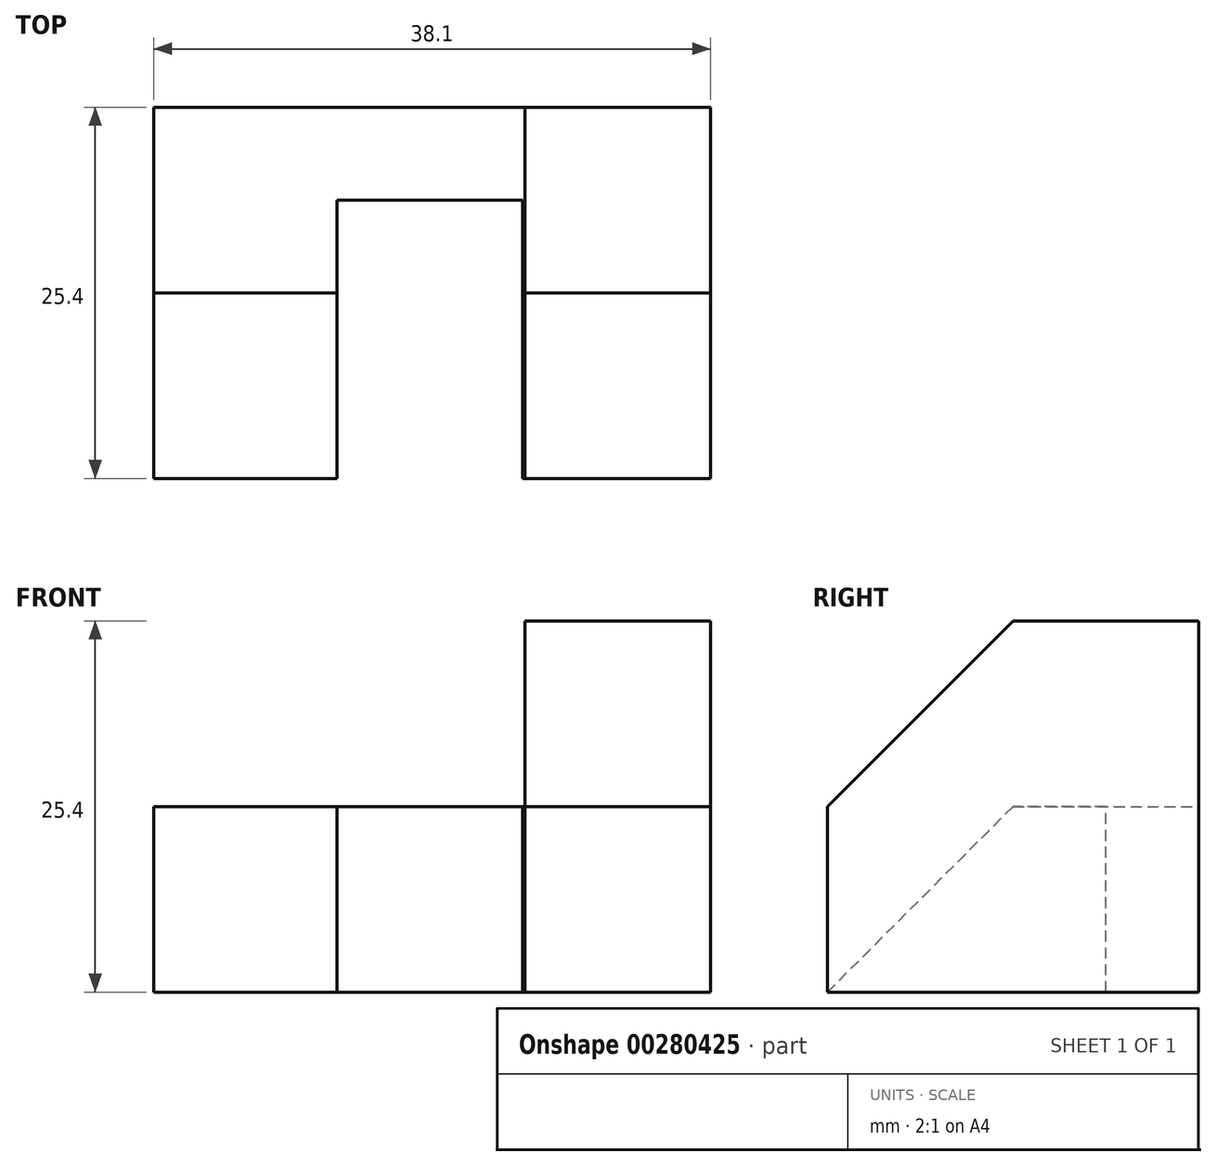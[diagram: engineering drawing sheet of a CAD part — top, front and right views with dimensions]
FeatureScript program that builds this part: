
annotation { "Feature Type Name" : "Feature", "Feature Type Description" : "" }
export const myFeature = defineFeature(function(context is Context, id is Id, definition is map)
    precondition{}
    {
        {
            var Q0;
            Q0=qCreatedBy(makeId("Front.planeOp"),FACE);
            var sketch = newSketch(context, id + "F0", { "sketchPlane" : qUnion([Q0])});
            skLineSegment(sketch, "E0", {"start": v(0, 0) * mm, "end": v(38.1, 0) * mm});
            skLineSegment(sketch, "E1", {"start": v(38.1, 0) * mm, "end": v(38.1, 25.4) * mm});
            skLineSegment(sketch, "E2", {"start": v(38.1, 25.4) * mm, "end": v(0, 25.4) * mm});
            skLineSegment(sketch, "E3", {"start": v(0, 25.4) * mm, "end": v(0, 0) * mm});
            skSolve(sketch);
        }
        {
            var Q0;
            Q0 = qSketchRegion(id + "F0", true);
            extrude(context, id + "F1", {"entities" : qUnion([Q0]), "depth" : 25.4 * mm, "symmetric" : true});
        }
        {
            var Q0;
            Q0=makeQuery(id+"F1.opExtrude","SWEPT_FACE",FACE,{"disambiguationData":[OSD([sQuery(id+"F0.wireOp",EDGE,"E2")])]});
            var sketch = newSketch(context, id + "F2", { "sketchPlane" : qUnion([Q0])});
            skLineSegment(sketch, "E4", {"start": v(19.05, -12.7) * mm, "end": v(12.54, -12.7) * mm});
            skLineSegment(sketch, "E5", {"start": v(12.54, -12.7) * mm, "end": v(12.54, 6.35) * mm});
            skLineSegment(sketch, "E6", {"start": v(12.54, 6.35) * mm, "end": v(25.24, 6.35) * mm});
            skLineSegment(sketch, "E7", {"start": v(25.24, 6.35) * mm, "end": v(25.24, -12.7) * mm});
            skLineSegment(sketch, "E8", {"start": v(25.24, -12.7) * mm, "end": v(12.54, -12.7) * mm});
            skSolve(sketch);
        }
        {
            var Q0;
            Q0 = qSketchRegion(id + "F2", true);
            extrude(context, id + "F3", {"entities" : qUnion([Q0]), "operationType" : NewBodyOperationType.REMOVE, "endBound" : BoundingType.THROUGH_ALL, "oppositeDirection" : true, "depth" : 25.4 * mm});
        }
        {
            var Q0;
            Q0=makeQuery(id+"F1.opExtrude","SWEPT_FACE",FACE,{"disambiguationData":[OSD([sQuery(id+"F0.wireOp",EDGE,"E1")])]});
            var sketch = newSketch(context, id + "F4", { "sketchPlane" : qUnion([Q0])});
            skLineSegment(sketch, "E9", {"start": v(-12.7, 25.4) * mm, "end": v(0, 25.4) * mm});
            skLineSegment(sketch, "E10", {"start": v(0, 25.4) * mm, "end": v(-12.7, 12.7) * mm});
            skLineSegment(sketch, "E11", {"start": v(-12.7, 12.7) * mm, "end": v(-12.7, 25.4) * mm});
            skSolve(sketch);
        }
        {
            var Q0;
            Q0 = qSketchRegion(id + "F4", true);
            extrude(context, id + "F5", {"entities" : qUnion([Q0]), "operationType" : NewBodyOperationType.REMOVE, "endBound" : BoundingType.UP_TO_NEXT, "oppositeDirection" : true, "depth" : 25.4 * mm});
        }
        {
            var Q0;
            Q0=makeQuery(id+"F1.opExtrude","SWEPT_FACE",FACE,{"disambiguationData":[OSD([sQuery(id+"F0.wireOp",EDGE,"E3")])]});
            var sketch = newSketch(context, id + "F6", { "sketchPlane" : qUnion([Q0])});
            skLineSegment(sketch, "E12", {"start": v(12.7, 25.4) * mm, "end": v(12.7, 12.7) * mm});
            skLineSegment(sketch, "E13", {"start": v(12.7, 12.7) * mm, "end": v(-12.7, 12.7) * mm});
            skLineSegment(sketch, "E14", {"start": v(-12.7, 12.7) * mm, "end": v(-12.7, 25.4) * mm});
            skLineSegment(sketch, "E15", {"start": v(-12.7, 25.4) * mm, "end": v(12.7, 25.4) * mm});
            skSolve(sketch);
        }
        {
            var Q0;
            Q0 = qSketchRegion(id + "F6", true);
            extrude(context, id + "F7", {"entities" : qUnion([Q0]), "operationType" : NewBodyOperationType.REMOVE, "oppositeDirection" : true, "depth" : 25.4 * mm});
        }
        {
            var Q0;
            Q0=makeQuery(id+"F1.opExtrude","SWEPT_FACE",FACE,{"disambiguationData":[OSD([sQuery(id+"F0.wireOp",EDGE,"E3")])]});
            var sketch = newSketch(context, id + "F8", { "sketchPlane" : qUnion([Q0])});
            skLineSegment(sketch, "E16", {"start": v(12.7, 0) * mm, "end": v(12.7, 12.7) * mm});
            skLineSegment(sketch, "E17", {"start": v(12.7, 12.7) * mm, "end": v(0, 12.7) * mm});
            skLineSegment(sketch, "E18", {"start": v(0, 12.7) * mm, "end": v(12.7, 0) * mm});
            skSolve(sketch);
        }
        {
            var Q0;
            Q0 = qSketchRegion(id + "F8", true);
            extrude(context, id + "F9", {"entities" : qUnion([Q0]), "operationType" : NewBodyOperationType.REMOVE, "oppositeDirection" : true, "depth" : 25.4 * mm});
        }
    });
